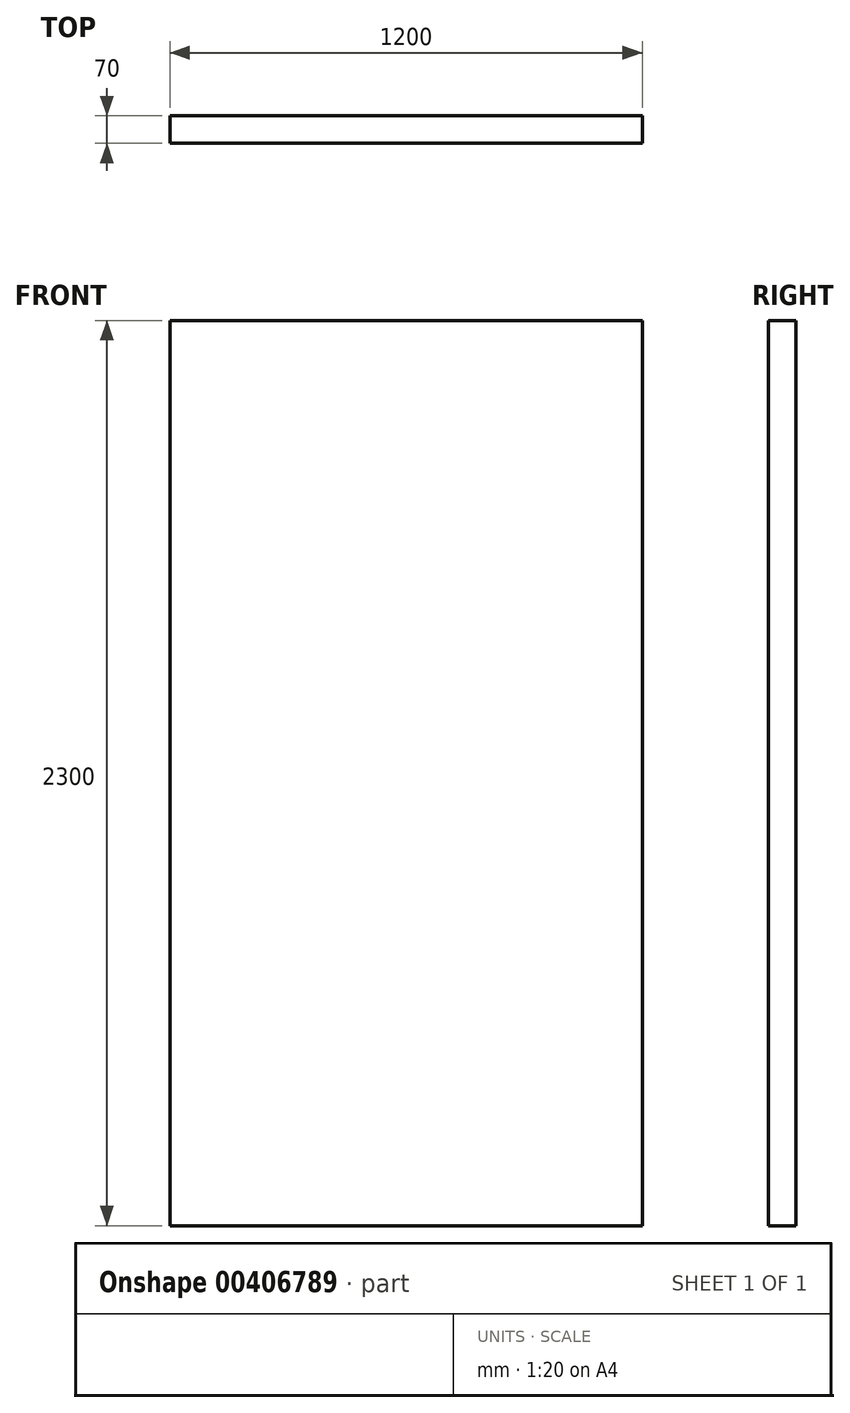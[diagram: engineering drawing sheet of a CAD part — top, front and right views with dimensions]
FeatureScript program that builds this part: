
annotation { "Feature Type Name" : "Feature", "Feature Type Description" : "" }
export const myFeature = defineFeature(function(context is Context, id is Id, definition is map)
    precondition{}
    {
        {
            var Q0;
            Q0=qCreatedBy(makeId("Front.planeOp"),FACE);
            var sketch = newSketch(context, id + "F0", { "sketchPlane" : qUnion([Q0])});
            skLineSegment(sketch, "E0.bottom", {"start": v(600, -1150) * mm, "end": v(-600, -1150) * mm});
            skLineSegment(sketch, "E0.top", {"start": v(600, 1150) * mm, "end": v(-600, 1150) * mm});
            skLineSegment(sketch, "E0.left", {"start": v(600, -1150) * mm, "end": v(600, 1150) * mm});
            skLineSegment(sketch, "E0.right", {"start": v(-600, -1150) * mm, "end": v(-600, 1150) * mm});
            skPoint(sketch, "E0.middle", {"position": v(0, 0) * mm});
            skSolve(sketch);
        }
        {
            var Q0;
            Q0=makeQuery(id+"F0.imprint","IMPRINT",FACE,{"disambiguationData":[TD([[makeQuery(id+"F0.imprint","IMPRINT",EDGE,{"derivedFrom":sQuery(id+"F0.wireOp",EDGE,"E0.bottom")}),-1.0]])]});
            extrude(context, id + "F1", {"entities" : qUnion([Q0]), "depth" : 70 * mm});
        }
    });
